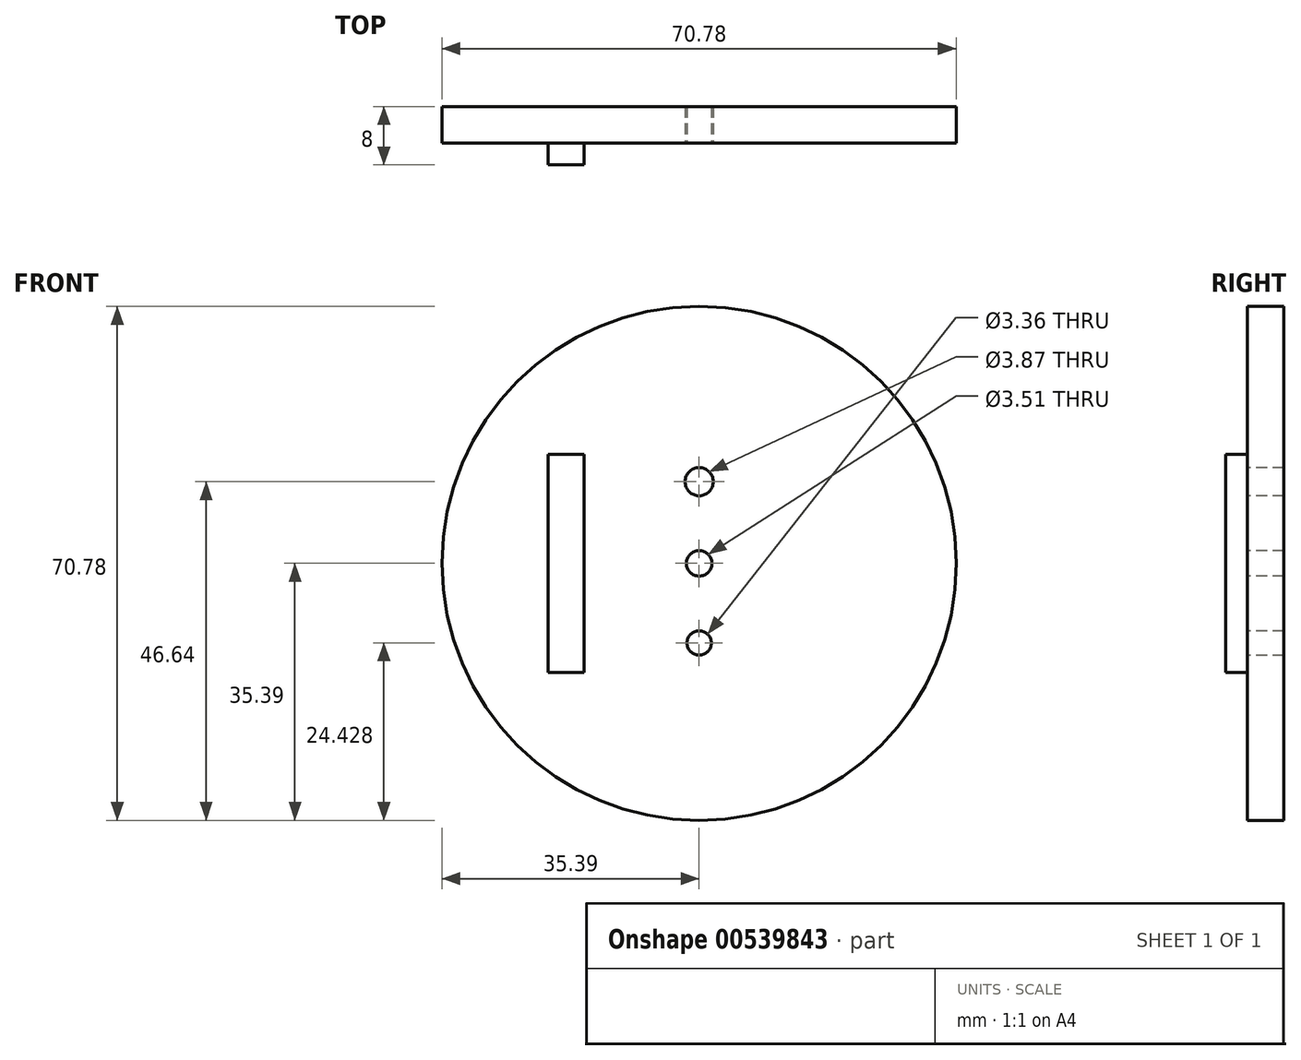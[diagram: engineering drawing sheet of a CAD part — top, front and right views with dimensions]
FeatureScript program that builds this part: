
annotation { "Feature Type Name" : "Feature", "Feature Type Description" : "" }
export const myFeature = defineFeature(function(context is Context, id is Id, definition is map)
    precondition{}
    {
        {
            var Q0;
            Q0=qCreatedBy(makeId("Front.planeOp"),FACE);
            var sketch = newSketch(context, id + "F0", { "sketchPlane" : qUnion([Q0])});
            skCircle(sketch, "E0", {"center": v(0, 0) * mm, "radius": 35.4 * mm});
            skSolve(sketch);
        }
        {
            var Q0;
            Q0=makeQuery(id+"F0.imprint","IMPRINT",FACE,{"disambiguationData":[TD([[makeQuery(id+"F0.imprint","IMPRINT",EDGE,{"derivedFrom":sQuery(id+"F0.wireOp",EDGE,"E0")}),1.0]])]});
            extrude(context, id + "F1", {"entities" : qUnion([Q0]), "depth" : 5 * mm, "offsetDistance" : 25 * mm});
        }
        {
            var Q0;
            Q0=makeQuery(id+"F1.opExtrude","CAP_FACE",FACE,{"disambiguationData":[OSD([sQuery(id+"F0.wireOp",EDGE,"E0")])],"isStart":false});
            var sketch = newSketch(context, id + "F2", { "sketchPlane" : qUnion([Q0])});
            skLineSegment(sketch, "E1.bottom", {"start": v(-20.77, 15) * mm, "end": v(-15.87, 15) * mm});
            skLineSegment(sketch, "E1.top", {"start": v(-20.77, -15) * mm, "end": v(-15.87, -15) * mm});
            skLineSegment(sketch, "E1.left", {"start": v(-20.77, 15) * mm, "end": v(-20.77, -15) * mm});
            skLineSegment(sketch, "E1.right", {"start": v(-15.87, 15) * mm, "end": v(-15.87, -15) * mm});
            skSolve(sketch);
        }
        {
            var Q0;
            Q0=makeQuery(id+"F1.opExtrude","CAP_FACE",FACE,{"disambiguationData":[OSD([sQuery(id+"F0.wireOp",EDGE,"E0")])],"isStart":false});
            var sketch = newSketch(context, id + "F3", { "sketchPlane" : qUnion([Q0])});
            skCircle(sketch, "E2", {"center": v(0, 11.25) * mm, "radius": 1.55 * mm});
            skCircle(sketch, "E3", {"center": v(0, -10.96) * mm, "radius": 1.68 * mm});
            skCircle(sketch, "E4", {"center": v(0, 0) * mm, "radius": 1.47 * mm});
            skSolve(sketch);
        }
        {
            var Q0;
            Q0=makeQuery(id+"F3.imprint","IMPRINT",FACE,{"disambiguationData":[TD([[makeQuery(id+"F3.imprint","IMPRINT",EDGE,{"derivedFrom":sQuery(id+"F3.wireOp",EDGE,"E3")}),1.0]])]});
            extrude(context, id + "F4", {"entities" : qUnion([Q0]), "operationType" : NewBodyOperationType.REMOVE, "oppositeDirection" : true, "depth" : 25 * mm, "offsetDistance" : 25 * mm});
        }
        {
            var Q0;
            Q0=makeQuery(id+"F1.opExtrude","CAP_FACE",FACE,{"disambiguationData":[OSD([sQuery(id+"F0.wireOp",EDGE,"E0")])],"isStart":false});
            var sketch = newSketch(context, id + "F5", { "sketchPlane" : qUnion([Q0])});
            skCircle(sketch, "E5", {"center": v(0, 11.25) * mm, "radius": 1.94 * mm});
            skSolve(sketch);
        }
        {
            var Q0;
            Q0=makeQuery(id+"F5.imprint","IMPRINT",FACE,{"disambiguationData":[TD([[makeQuery(id+"F5.imprint","IMPRINT",EDGE,{"derivedFrom":sQuery(id+"F5.wireOp",EDGE,"E5")}),1.0]])]});
            extrude(context, id + "F6", {"entities" : qUnion([Q0]), "operationType" : NewBodyOperationType.REMOVE, "oppositeDirection" : true, "depth" : 25 * mm, "offsetDistance" : 25 * mm});
        }
        {
            var Q0;
            Q0=makeQuery(id+"F1.opExtrude","CAP_FACE",FACE,{"disambiguationData":[OSD([sQuery(id+"F0.wireOp",EDGE,"E0")])],"isStart":false});
            var sketch = newSketch(context, id + "F7", { "sketchPlane" : qUnion([Q0])});
            skCircle(sketch, "E6", {"center": v(0, 0) * mm, "radius": 1.75 * mm});
            skSolve(sketch);
        }
        {
            var Q0;
            Q0=makeQuery(id+"F7.imprint","IMPRINT",FACE,{"disambiguationData":[TD([[makeQuery(id+"F7.imprint","IMPRINT",EDGE,{"derivedFrom":sQuery(id+"F7.wireOp",EDGE,"E6")}),1.0]])]});
            extrude(context, id + "F8", {"entities" : qUnion([Q0]), "operationType" : NewBodyOperationType.REMOVE, "oppositeDirection" : true, "depth" : 25 * mm, "offsetDistance" : 25 * mm});
        }
        {
            var Q0;
            Q0 = qSketchRegion(id + "F2", true);
            extrude(context, id + "F9", {"entities" : qUnion([Q0]), "operationType" : NewBodyOperationType.ADD, "depth" : 3 * mm, "offsetDistance" : 25 * mm});
        }
    });
